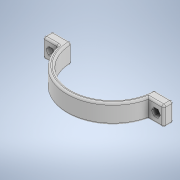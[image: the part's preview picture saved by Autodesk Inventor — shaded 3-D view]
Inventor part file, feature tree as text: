
AUTODESK INVENTOR PART (.ipt)
format: ipt  version: 2020 (Build 240168000, 168)  size: 230,912 bytes
history: native  units: in
note: dims shown in document units (in); Inventor stores cm internally (conversion verified against a paired STEP export)
features: sketch x5, extrude x4, mirror x2, shell x1, plane x1, hole x1, fillet x1
ambient origin geometry x8: Origin, YZ Plane, XZ Plane, XY Plane, X Axis, Y Axis, Z Axis, Center Point
bodies: Solid1 (feature_tree)
feature tree (15):
  extrude  "Extrusion1"  Depth=0.7874in TaperAngle=0.0deg
  shell  "Shell1"  Thickness=0.1969in
  extrude  "Extrusion2"  [1 undecoded]
  plane  "Work Plane1"
  extrude  "Extrusion3"  Depth=0.3937in
  mirror  "Mirror1"
  extrude  "Extrusion4"  Depth=0.0787in
  hole  "Hole3"  [1 undecoded]
  mirror  "Mirror3"
  fillet  "Fillet1"  [1 undecoded]
  sketch  "Sketch1"  dims[d0=3.7402in d1=0.7874in d2=0.0in d3=0.1969in]
  sketch  "Sketch2"  dims[d4=0.3937in d5=0.0in d6=-1.8701in]
  sketch  "Sketch3"  dims[d7=0.7874in d8=0.3937in]
  sketch  "Sketch6"  dims[d9=0.0787in d10=0.5906in d11=0.0in d12=0.0in d27=0.315in]
  sketch  "Sketch7"  dims[d28=0.1969in d29=0.0in d30=0.2165in d31=0.2362in d32=0.4819in d33=0.1409in d34=0.5635in d35=0.315in d36=0.8108in d37=0.0787in]
note: 3 required parameter values undecoded (feature->parameter linkage not recoverable at this tier; creation-order binding heuristic only, values carry confidence <= 0.55)
